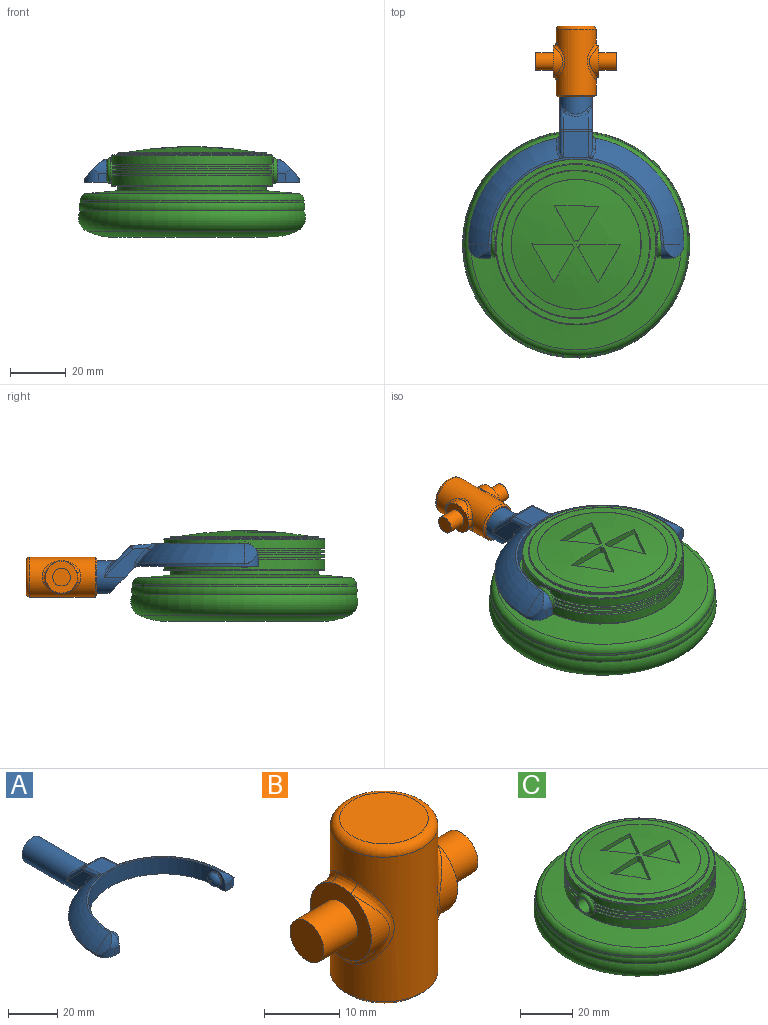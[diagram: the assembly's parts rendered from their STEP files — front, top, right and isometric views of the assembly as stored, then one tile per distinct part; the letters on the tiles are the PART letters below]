
ASSEMBLY  parts=3 mates=2
PART A: 48 faces, bbox 77.3x80.8x18.2 mm
  f0: plane 11.99x9.83mm, normal (0,-0.71,-0.71), area 141.5mm2, adj f1,f2,f9,f30,f43,f46
  f1: plane 15.39x10.49mm, normal (-1,0,0), area 63.5mm2, adj f0,f30,f32,f36,f46,f47
  f2: plane 15.39x10.49mm, normal (1,0,0), area 63.5mm2, adj f0,f30,f34,f39,f43,f44
  f3: plane 9.14x6.37mm, normal (0,0.71,0.71), area 67.6mm2, adj f35,f36,f39,f40
  f4: cylinder r=38.61mm len=37.99mm, axis (0,0,-1), area 42.6mm2, adj f6,f9,f17,f46,f47
  f5: torus R=19.3mm, axis (0,0,-1), area 507.8mm2, adj f10,f11,f12,f29,f42,f44
  f6: torus R=19.3mm, axis (0,0,-1), area 507.8mm2, adj f4,f11,f15,f28,f45,f47
  f7: cylinder r=30.48mm len=60.96mm, axis (0,0,-1), area 746.6mm2, adj f8,f9,f11,f14,f21,f24
  f8: plane 8.13x5.08mm, normal (-1,0,0), area 19.9mm2, adj f7,f9,f13,f19,f24
  f9: plane 77.22x43.73mm, normal (0,0,-1), area 956.2mm2, adj f0,f4,f7,f8,f10,f13,f14,f16
  f10: cylinder r=38.61mm len=37.99mm, axis (0,0,-1), area 42.6mm2, adj f5,f9,f20,f43,f44
  f11: plane 62.55x30.95mm, normal (0,0,1), area 75mm2, adj f5,f6,f7,f18,f19,f27
  f12: cylinder r=22.71mm len=7.33mm, axis (0,1,0), area 24.8mm2, adj f5,f19,f20
  f13: plane 3.05x3.05mm, normal (0,-1,0), area 9.3mm2, adj f8,f9,f19,f20
  f14: plane 8.13x5.08mm, normal (1,0,0), area 19.9mm2, adj f7,f9,f16,f18,f21
  f15: cylinder r=22.71mm len=7.33mm, axis (0,1,0), area 24.8mm2, adj f6,f17,f18
  f16: plane 3.05x3.05mm, normal (0,-1,0), area 9.3mm2, adj f9,f14,f17,f18
  f17: cylinder r=5.08mm len=5.08mm, axis (0,0,-1), area 21.9mm2, adj f4,f9,f15,f16,f18
  f18: cylinder r=5.08mm len=5.08mm, axis (-1,0,0), area 21.9mm2, adj f11,f14,f15,f16,f17
  f19: cylinder r=5.08mm len=5.08mm, axis (-1,0,0), area 21.9mm2, adj f8,f11,f12,f13,f20
  f20: cylinder r=5.08mm len=5.08mm, axis (0,0,-1), area 21.9mm2, adj f9,f10,f12,f13,f19
  f21: cylinder r=3.17mm len=6.35mm, axis (-1,0,0), area 12.7mm2, adj f7,f14,f23
  f22: plane 1.27x1.27mm, normal (1,0,0), area 1.3mm2, adj f23
  f23: torus R=0.64mm, axis (1,0,0), area 56.5mm2, adj f21,f22
  f24: cylinder r=3.17mm len=6.35mm, axis (1,0,0), area 12.7mm2, adj f7,f8,f26
  f25: plane 1.27x1.27mm, normal (-1,0,0), area 1.3mm2, adj f26
  f26: torus R=0.64mm, axis (-1,0,0), area 56.5mm2, adj f24,f25
  f27: plane 9.86x9.36mm, normal (0,0.09,1), area 85.6mm2, adj f11,f28,f29,f32,f34,f35,f42,f45
  f28: plane 1.04x0.17mm, normal (0,-1,0), area 0mm2, adj f6,f27,f45
  f29: plane 1.04x0.17mm, normal (0,-1,0), area 0mm2, adj f5,f27,f42
  f30: cylinder r=5.84mm len=33.01mm, axis (0,-1,0), area 1029.7mm2, adj f0,f1,f2,f31,f38,f40,f41
  f31: plane 11.68x11.68mm, normal (0,1,0), area 107.2mm2, adj f30
  f32: cylinder r=1.27mm len=9.13mm, axis (0,-1,0.09), area 14.4mm2, adj f1,f27,f33,f45
  f33: sphere r=1.27mm, area 1.5mm2, adj f32,f35,f36
  f34: cylinder r=1.27mm len=9.13mm, axis (0,1,-0.09), area 14.4mm2, adj f2,f27,f37,f42
  f35: cylinder r=1.27mm len=9.14mm, axis (-1,0,0), area 8.1mm2, adj f3,f27,f33,f37
  f36: cylinder r=1.27mm len=10.91mm, axis (0,-0.71,0.71), area 23.1mm2, adj f1,f3,f33,f38
  f37: sphere r=1.27mm, area 1.5mm2, adj f34,f35,f39
  f38: bspline ~4.55x2.75mm, area 2.3mm2, adj f30,f36,f40
  f39: cylinder r=1.27mm len=10.91mm, axis (0,0.71,-0.71), area 23.1mm2, adj f2,f3,f37,f41
  f40: bspline ~9.14x2.56mm, area 10.7mm2, adj f3,f30,f38,f41
  f41: bspline ~5.23x3.53mm, area 2.3mm2, adj f30,f39,f40
  f42: bspline ~4.62x3.14mm, area 5.2mm2, adj f5,f27,f29,f34,f44
  f43: cylinder r=1.27mm len=1.74mm, axis (0,0,-1), area 1.9mm2, adj f0,f2,f9,f10,f44
  f44: bspline ~8.6x7.86mm, area 11.9mm2, adj f2,f5,f10,f42,f43
  f45: bspline ~4.62x3.14mm, area 5.2mm2, adj f6,f27,f28,f32,f47
  f46: cylinder r=1.27mm len=1.74mm, axis (0,0,-1), area 1.9mm2, adj f0,f1,f4,f9,f47
  f47: bspline ~8.6x7.86mm, area 11.9mm2, adj f1,f4,f6,f45,f46
PART B: 25 faces, bbox 28.9x15.5x25.4 mm
  f0: cylinder r=5.71mm len=10.81mm, axis (-1,0,0), area 26.2mm2, adj f5,f15
  f1: cylinder r=5.71mm len=10.81mm, axis (-1,0,0), area 26.2mm2, adj f8,f11
  f2: cylinder r=7.14mm len=23.5mm, axis (0,0,-1), area 763.2mm2, adj f9,f10,f11,f12,f13,f14,f15,f16
  f3: plane 11.75x11.75mm, normal (0,0,1), area 108.4mm2, adj f17
  f4: plane 13.02x13.02mm, normal (0,0,-1), area 16.3mm2, adj f22,f24
  f5: plane 11.46x11.46mm, normal (1,0,0), area 70.9mm2, adj f0,f6,f13,f16,f18
  f6: cylinder r=5.71mm len=10.81mm, axis (-1,0,0), area 26.2mm2, adj f5,f14
  f7: cylinder r=5.71mm len=10.81mm, axis (-1,0,0), area 26.2mm2, adj f8,f10
  f8: plane 11.46x11.46mm, normal (-1,0,0), area 70.9mm2, adj f1,f7,f9,f12,f20
  f9: bspline ~4.64x1.73mm, area 6.5mm2, adj f2,f8,f10,f11
  f10: bspline ~13.62x4.91mm, area 20.7mm2, adj f2,f7,f9,f12
  f11: bspline ~13.6x4.87mm, area 20.7mm2, adj f1,f2,f9,f12
  f12: bspline ~4.64x1.73mm, area 6.5mm2, adj f2,f8,f10,f11
  f13: bspline ~4.64x1.73mm, area 6.5mm2, adj f2,f5,f14,f15
  f14: bspline ~13.62x4.91mm, area 20.7mm2, adj f2,f6,f13,f16
  f15: bspline ~13.6x4.87mm, area 20.7mm2, adj f0,f2,f13,f16
  f16: bspline ~4.64x1.73mm, area 6.5mm2, adj f2,f5,f14,f15
  f17: torus R=5.87mm, axis (0,0,1), area 83.8mm2, adj f2,f3
  f18: cylinder r=3.17mm len=6.35mm, axis (-1,0,0), area 126.7mm2, adj f5,f19
  f19: plane 6.35x6.35mm, normal (1,0,0), area 31.7mm2, adj f18
  f20: cylinder r=3.17mm len=6.35mm, axis (1,0,0), area 126.7mm2, adj f8,f21
  f21: plane 6.35x6.35mm, normal (-1,0,0), area 31.7mm2, adj f20
  f22: cylinder r=6.1mm len=22.86mm, axis (0,0,-1), area 875.6mm2, adj f4,f23
  f23: plane 12.19x12.19mm, normal (0,0,-1), area 116.7mm2, adj f22
  f24: cone r=7.14mm half-angle=45deg, axis (0,0,1), area 38.5mm2, adj f2,f4
PART C: 64 faces, bbox 96.3x96.3x32.5 mm
  f0: cylinder r=28.87mm len=57.73mm, axis (0,0,-1), area 648mm2, adj f5,f6,f54,f55,f60
  f1: plane 57.04x24.4mm, normal (0,0,-1), area 101.2mm2, adj f4,f8,f54,f55
  f2: plane 57.04x24.4mm, normal (0,0,-1), area 101.2mm2, adj f3,f7,f54,f55
  f3: cylinder r=27.6mm len=54.52mm, axis (0,0,-1), area 49.5mm2, adj f2,f6,f54,f55
  f4: cylinder r=27.6mm len=54.52mm, axis (0,0,-1), area 49.5mm2, adj f1,f5,f54,f55
  f5: plane 57.09x24.58mm, normal (0,0,1), area 101.7mm2, adj f0,f4,f54,f55
  f6: plane 57.09x24.58mm, normal (0,0,1), area 101.7mm2, adj f0,f3,f54,f55
  f7: cylinder r=28.87mm len=57.04mm, axis (0,0,-1), area 77.7mm2, adj f2,f14,f54,f55
  f8: cylinder r=28.87mm len=57.04mm, axis (0,0,-1), area 77.7mm2, adj f1,f13,f54,f55
  f9: plane 57.02x24.34mm, normal (0,0,-1), area 101.1mm2, adj f12,f16,f54,f55
  f10: plane 57.02x24.34mm, normal (0,0,-1), area 101.1mm2, adj f11,f15,f54,f55
  f11: cylinder r=27.6mm len=54.45mm, axis (0,0,-1), area 49.2mm2, adj f10,f14,f54,f55
  f12: cylinder r=27.6mm len=54.45mm, axis (0,0,-1), area 49.2mm2, adj f9,f13,f54,f55
  f13: plane 57.01x24.3mm, normal (0,0,1), area 101mm2, adj f8,f12,f54,f55
  f14: plane 57.01x24.3mm, normal (0,0,1), area 101mm2, adj f7,f11,f54,f55
  f15: cylinder r=28.87mm len=57.09mm, axis (0,0,-1), area 78mm2, adj f10,f18,f54,f55
  f16: cylinder r=28.87mm len=57.09mm, axis (0,0,-1), area 78mm2, adj f9,f17,f54,f55
  f17: plane 57.09x24.58mm, normal (0,0,1), area 101.7mm2, adj f16,f22,f54,f55
  f18: plane 57.09x24.58mm, normal (0,0,1), area 101.7mm2, adj f15,f21,f54,f55
  f19: plane 57.18x24.87mm, normal (0,0,-1), area 102.5mm2, adj f22,f23,f54,f55
  f20: plane 57.18x24.87mm, normal (0,0,-1), area 102.5mm2, adj f21,f23,f54,f55
  f21: cylinder r=27.6mm len=54.61mm, axis (0,0,-1), area 49.8mm2, adj f18,f20,f54,f55
  f22: cylinder r=27.6mm len=54.61mm, axis (0,0,-1), area 49.8mm2, adj f17,f19,f54,f55
  f23: cylinder r=28.87mm len=57.73mm, axis (0,0,-1), area 543.4mm2, adj f19,f20,f54,f55,f61
  f24: sphere r=135.39mm, area 1385.3mm2, adj f38,f39,f40,f41,f43,f44,f45,f46
  f25: plane 39.35x39.35mm, normal (0,0,-1), area 1216.2mm2, adj f26
  f26: torus R=20.13mm, axis (0,0,-1), area 1430.4mm2, adj f25,f27
  f27: torus R=27.75mm, axis (0,0,-1), area 3543.7mm2, adj f26,f28
  f28: torus R=35.37mm, axis (0,0,-1), area 2180.8mm2, adj f27,f29
  f29: torus R=37.36mm, axis (0,0,-1), area 734.8mm2, adj f28,f30
  f30: cylinder r=40.07mm len=80.14mm, axis (0,0,-1), area 213.4mm2, adj f29,f34
  f31: cone r=26.58mm half-angle=85deg, axis (0,0,-1), area 2265.9mm2, adj f32,f34
  f32: cylinder r=26.58mm len=53.16mm, axis (0,0,-1), area 265.1mm2, adj f31,f33
  f33: plane 57.23x57.23mm, normal (0,0,-1), area 352.3mm2, adj f32,f60
  f34: torus R=37.53mm, axis (0,0,1), area 928.9mm2, adj f30,f31
  f35: cone r=26.58mm half-angle=87deg, axis (0,0,-1), area 477.5mm2, adj f62,f63
  f36: cylinder r=26.58mm len=53.16mm, axis (0,0,-1), area 92.3mm2, adj f37,f62
  f37: plane 57.23x57.23mm, normal (0,0,1), area 352.3mm2, adj f36,f61
  f38: cylinder r=1.27mm len=2.53mm, axis (0,0,1), area 3.4mm2, adj f24,f39,f41,f42
  f39: plane 14.6x2.53mm, normal (-0.01,-1,0), area 32.2mm2, adj f24,f38,f40,f42
  f40: plane 13.81x7.83mm, normal (0.87,0.49,0), area 28mm2, adj f24,f39,f41,f42
  f41: plane 12.59x7.4mm, normal (-0.86,0.51,0), area 32.2mm2, adj f24,f38,f40,f42
  f42: plane 15.23x13.81mm, normal (0,0,1), area 108.3mm2, adj f38,f39,f40,f41
  f43: cylinder r=1.27mm len=2.53mm, axis (0,0,1), area 3.4mm2, adj f24,f44,f46,f47
  f44: plane 12.7x7.21mm, normal (0.87,0.49,0), area 32.1mm2, adj f24,f43,f45,f47
  f45: plane 13.69x8.04mm, normal (-0.86,0.51,0), area 27.9mm2, adj f24,f44,f46,f47
  f46: plane 14.6x2.53mm, normal (-0.01,-1,0), area 32.1mm2, adj f24,f43,f45,f47
  f47: plane 15.25x13.8mm, normal (0,0,1), area 108.3mm2, adj f43,f44,f45,f46
  f48: plane 15.87x1.84mm, normal (-0.01,-1,0), area 28mm2, adj f24,f49,f51,f52
  f49: plane 12.7x7.21mm, normal (0.87,0.49,0), area 32.2mm2, adj f24,f48,f50,f52
  f50: cylinder r=1.27mm len=2.53mm, axis (0,0,1), area 3.4mm2, adj f24,f49,f51,f52
  f51: plane 12.59x7.4mm, normal (-0.86,0.51,0), area 32.2mm2, adj f24,f48,f50,f52
  f52: plane 15.87x12.71mm, normal (0,0,1), area 108.3mm2, adj f48,f49,f50,f51
  f53: plane 6.6x6.6mm, normal (1,0,0), area 2.6mm2, adj f58,f59
  f54: cylinder r=4.57mm len=9.14mm, axis (-1,0,0), area 20.2mm2, adj f0,f1,f2,f3,f4,f5,f6,f7
  f55: cylinder r=4.57mm len=9.14mm, axis (-1,0,0), area 20.2mm2, adj f0,f1,f2,f3,f4,f5,f6,f7
  f56: plane 6.6x6.6mm, normal (-1,0,0), area 2.6mm2, adj f57,f59
  f57: torus R=3.3mm, axis (1,0,0), area 51.5mm2, adj f55,f56
  f58: torus R=3.3mm, axis (1,0,0), area 51.5mm2, adj f53,f54
  f59: cylinder r=3.17mm len=60.96mm, axis (1,0,0), area 1216.1mm2, adj f53,f56
  f60: torus R=28.61mm, axis (0,0,1), area 72.1mm2, adj f0,f33
  f61: torus R=28.61mm, axis (0,0,-1), area 72.1mm2, adj f23,f37
  f62: torus R=26.33mm, axis (0,0,1), area 64.2mm2, adj f35,f36
  f63: torus R=23.29mm, axis (0,0,1), area 4.5mm2, adj f24,f35
PLACE A t=(32.34,27.52,20.85)mm
PLACE B rot(axis=(-1,0,0),90deg) t=(32.34,80.3,16.88)mm
PLACE C t=(32.34,27.52,33.52)mm
MATE revolute A.f24 <-> C.f54  axis (-1,0,0) through (62.82,27.52,24.92)mm
MATE revolute B.f2 <-> A.f30  axis (0,-1,0) through (32.34,103.16,16.88)mm
